# Revit family: E_Wall Junction Box_F_MEPcontent_Spelsberg_RK-RKA-ALR-AKi-R_INT-EN
name_source: partatom
category: Elektroinstallationen
revit_build: Autodesk Revit 2017 (Build: 20160225_1515(x64)
units: mm (PartAtom-declared; Revit-internal decimal feet)

## family parameters
Basisbauteil = Fläche
Beim Laden mit Abzugskörper schneiden = Nein
Bemaßung runder Anschluss = Durchmesser verwenden
Beschriftungsausrichtung beibehalten = Ja
Gemeinsam genutzt = Nein
OmniClass-Nummer = 23.80.30.14.24
OmniClass-Titel = Junction Boxes
Raumberechnungspunkt = Nein
Teiletyp = Verteilerkasten

## types (110) — shared parameters
Beschreibung = Terminal block enclosure RKK 4/07-7x4²
ETIM Article Class = EC000261
Hersteller = Spelsberg
IFCExportAs = IfcJunctionBox
IFCExportType = NOTDEFINED
Manufacturer URL = http://www.spelsberg.com
Modell = RKK 4/07-7x4²
Placeholder Height = 5 mm  [stored 0.0164042 ft]
Product Line = Spelsberg
Revit Version = 2017
Rotation U-Axis Correction = 0.00°
Rotation U-Axis Default Correction = 0.00°
Rotation V-Axis Correction = 0.00°
Rotation V-Axis Default Correction = 0.00°
Rotation W-Axis Correction = 0.00°
Rotation W-Axis Default Correction = 0.00°
URL = www.stabiplan.com
Void Diameter = 4 mm  [stored 0.0131234 ft]
zero-valued in all types: Main Screw Condition, Vorgabe-Ansicht

## per-type parameters (varying)
| type | Article Description | Body | Cap | Cap Height | Height | Horizontal Third Screw | Length | Manufacturer Art. No. | Vertical Third Screw | Width |
| AKi-R 4/136-SL | Terminal block enclosure AKi-R 4/136-SL | Color RGB 197-199-196 | Color RGB 197-199-196 | 38 mm  [stored 0.124672 ft] | 132 mm  [stored 0.433071 ft] | Nein | 600 mm | 74313601 | Ja | 300 mm |
| AKi-R 4/102-SL | Terminal block enclosure AKi-R 4/102-SL | Color RGB 197-199-196 | Color RGB 197-199-196 | 38 mm  [stored 0.124672 ft] | 132 mm  [stored 0.433071 ft] | Nein | 450 mm | 74310201 | Nein | 300 mm |
| AKi-R 4/68-SL | Terminal block enclosure AKi-R 4/68-SL | Color RGB 140-150-157 | Color RGB 140-150-157 | 38 mm  [stored 0.124672 ft] | 132 mm  [stored 0.433071 ft] | Nein | 300 mm | 74306801 | Nein | 300 mm |
| AKi-R 4/34-SL | Terminal block enclosure AKi-R 4/34-SL | Color RGB 140-150-157 | Color RGB 140-150-157 | 38 mm  [stored 0.124672 ft] | 132 mm  [stored 0.433071 ft] | Nein | 150 mm | 74303401 | Nein | 300 mm |
| AKi-R 4/136 | Terminal block enclosure AKi-R 4/136 | Color RGB 197-199-196 | Color RGB 197-199-196 | 38 mm  [stored 0.124672 ft] | 132 mm  [stored 0.433071 ft] | Nein | 600 mm | 74213601 | Ja | 300 mm |
| AKi-R 4/102 | Terminal block enclosure AKi-R 4/102 | Color RGB 197-199-196 | Color RGB 197-199-196 | 38 mm  [stored 0.124672 ft] | 132 mm  [stored 0.433071 ft] | Nein | 450 mm | 74210201 | Nein | 300 mm |
| AKi-R 4/68 | Terminal block enclosure AKi-R 4/68 | Color RGB 197-199-196 | Color RGB 197-199-196 | 38 mm  [stored 0.124672 ft] | 132 mm  [stored 0.433071 ft] | Nein | 300 mm | 74206801 | Nein | 300 mm |
| AKi-R 4/34 | Terminal block enclosure AKi-R 4/34 | Color RGB 197-199-196 | Color RGB 197-199-196 | 38 mm  [stored 0.124672 ft] | 132 mm  [stored 0.433071 ft] | Nein | 150 mm | 74203401 | Nein | 300 mm |
| AKi-R 4/136-L | Empty enclosure AKi-R 4/136-L | Color RGB 197-199-196 | Color RGB 197-199-196 | 38 mm  [stored 0.124672 ft] | 132 mm  [stored 0.433071 ft] | Nein | 600 mm | 74190401 | Ja | 300 mm |
| AKi-R 4/102-L | Empty enclosure AKi-R 4/102-L | Color RGB 140-150-157 | Color RGB 140-150-157 | 38 mm  [stored 0.124672 ft] | 132 mm  [stored 0.433071 ft] | Nein | 450 mm | 74190301 | Nein | 300 mm |
| AKi-R 4/68-L | Empty enclosure AKi-R 4/68-L | Color RGB 140-150-157 | Color RGB 140-150-157 | 38 mm  [stored 0.124672 ft] | 132 mm  [stored 0.433071 ft] | Nein | 300 mm | 74190201 | Nein | 300 mm |
| AKi-R 4/34-L | Empty enclosure AKi-R 4/34-L | Color RGB 140-150-157 | Color RGB 140-150-157 | 38 mm  [stored 0.124672 ft] | 132 mm  [stored 0.433071 ft] | Nein | 150 mm | 74190101 | Nein | 300 mm |
| ALR 3323-L | Terminal block enclosure ALR 3323-L | Color RGB 140-150-157 | Color RGB 140-150-157 | 20 mm  [stored 0.0656168 ft] | 111 mm | Nein | 230 mm  [stored 0.754593 ft] | 16091601 | Nein | 330 mm |
| ALR 2823-L | Terminal block enclosure ALR 2823-L | Color RGB 140-150-157 | Color RGB 140-150-157 | 20 mm  [stored 0.0656168 ft] | 111 mm | Nein | 230 mm  [stored 0.754593 ft] | 16091501 | Nein | 280 mm |
| ALR 2320-L | Terminal block enclosure ALR 2320-L | Color RGB 140-150-157 | Color RGB 140-150-157 | 20 mm  [stored 0.0656168 ft] | 111 mm | Nein | 200 mm  [stored 0.656168 ft] | 16091401 | Nein | 230 mm  [stored 0.754593 ft] |
| ALR 3616-L | Terminal block enclosure ALR 3616-L | Color RGB 140-150-157 | Color RGB 140-150-157 | 20 mm  [stored 0.0656168 ft] | 91 mm  [stored 0.298556 ft] | Nein | 160 mm  [stored 0.524934 ft] | 16091301 | Nein | 360 mm |
| ALR 2616-L | Terminal block enclosure ALR 2616-L | Color RGB 140-150-157 | Color RGB 140-150-157 | 20 mm  [stored 0.0656168 ft] | 91 mm  [stored 0.298556 ft] | Nein | 160 mm  [stored 0.524934 ft] | 16091201 | Nein | 260 mm  [stored 0.853018 ft] |
| ALR 1616-L | Terminal block enclosure ALR 1616-L | Color RGB 140-150-157 | Color RGB 140-150-157 | 20 mm  [stored 0.0656168 ft] | 91 mm  [stored 0.298556 ft] | Nein | 160 mm  [stored 0.524934 ft] | 16091101 | Nein | 160 mm  [stored 0.524934 ft] |
| ALR 2212-L | Terminal block enclosure ALR 2212-L | Color RGB 140-150-157 | Color RGB 140-150-157 | 20 mm  [stored 0.0656168 ft] | 81 mm  [stored 0.265748 ft] | Nein | 120 mm  [stored 0.393701 ft] | 16091001 | Nein | 220 mm  [stored 0.721785 ft] |
| ALR 1212-L | Terminal block enclosure ALR 1212-L | Color RGB 140-150-157 | Color RGB 140-150-157 | 20 mm  [stored 0.0656168 ft] | 81 mm  [stored 0.265748 ft] | Nein | 120 mm  [stored 0.393701 ft] | 16090901 | Nein | 122 mm  [stored 0.400262 ft] |
| ALR 3323-4² | Terminal block enclosure ALR 3323-4² | Color RGB 140-150-157 | Color RGB 140-150-157 | 20 mm  [stored 0.0656168 ft] | 111 mm | Nein | 230 mm  [stored 0.754593 ft] | 16041601 | Nein | 330 mm |
| ALR 2823-4² | Terminal block enclosure ALR 2823-4² | Color RGB 140-150-157 | Color RGB 140-150-157 | 20 mm  [stored 0.0656168 ft] | 111 mm | Nein | 230 mm  [stored 0.754593 ft] | 16041501 | Nein | 280 mm |
| ALR 2320-4² | Terminal block enclosure ALR 2320-4² | Color RGB 140-150-157 | Color RGB 140-150-157 | 20 mm  [stored 0.0656168 ft] | 111 mm | Nein | 200 mm  [stored 0.656168 ft] | 16041401 | Nein | 230 mm  [stored 0.754593 ft] |
| ALR 3616-4² | Terminal block enclosure ALR 3616-4² | Color RGB 140-150-157 | Color RGB 140-150-157 | 20 mm  [stored 0.0656168 ft] | 91 mm  [stored 0.298556 ft] | Nein | 160 mm  [stored 0.524934 ft] | 16041301 | Nein | 360 mm |
| ALR 2616-4² | Terminal block enclosure ALR 2616-4² | Color RGB 140-150-157 | Color RGB 140-150-157 | 20 mm  [stored 0.0656168 ft] | 91 mm  [stored 0.298556 ft] | Nein | 160 mm  [stored 0.524934 ft] | 16041201 | Nein | 260 mm  [stored 0.853018 ft] |
| ALR 1616-4² | Terminal block enclosure ALR 1616-4² | Color RGB 140-150-157 | Color RGB 140-150-157 | 20 mm  [stored 0.0656168 ft] | 91 mm  [stored 0.298556 ft] | Nein | 160 mm  [stored 0.524934 ft] | 16041101 | Nein | 160 mm  [stored 0.524934 ft] |
| ALR 2212-4² | Terminal block enclosure ALR 2212-4² | Color RGB 140-150-157 | Color RGB 140-150-157 | 20 mm  [stored 0.0656168 ft] | 81 mm  [stored 0.265748 ft] | Nein | 120 mm  [stored 0.393701 ft] | 16041001 | Nein | 220 mm  [stored 0.721785 ft] |
| ALR 1212-4² | Terminal block enclosure ALR 1212-4² | Color RGB 140-150-157 | Color RGB 140-150-157 | 20 mm  [stored 0.0656168 ft] | 81 mm  [stored 0.265748 ft] | Nein | 120 mm  [stored 0.393701 ft] | 16040901 | Nein | 122 mm  [stored 0.400262 ft] |
| ALR 1010-4² | Terminal block enclosure ALR 1010-4² | Color RGB 140-150-157 | Color RGB 140-150-157 | 20 mm  [stored 0.0656168 ft] | 81 mm  [stored 0.265748 ft] | Nein | 100 mm  [stored 0.328084 ft] | 16040801 | Nein | 100 mm  [stored 0.328084 ft] |
| ALR 1808-4² | Terminal block enclosure ALR 1808-4² | Color RGB 140-150-157 | Color RGB 140-150-157 | 15 mm  [stored 0.0492126 ft] | 57 mm  [stored 0.187008 ft] | Nein | 80 mm  [stored 0.262467 ft] | 16040701 | Nein | 175 mm  [stored 0.574147 ft] |
| ALR 1308-4² | Terminal block enclosure ALR 1308-4² | Color RGB 140-150-157 | Color RGB 140-150-157 | 15 mm  [stored 0.0492126 ft] | 57 mm  [stored 0.187008 ft] | Nein | 80 mm  [stored 0.262467 ft] | 16040601 | Nein | 125 mm  [stored 0.410105 ft] |
| ALR 88-4² | Terminal block enclosure ALR 88-4² | Color RGB 140-150-157 | Color RGB 140-150-157 | 15 mm  [stored 0.0492126 ft] | 57 mm  [stored 0.187008 ft] | Nein | 80 mm  [stored 0.262467 ft] | 16040501 | Nein | 75 mm |
| RKA 4/136-L | Empty enclosure RKA 4/136-L | Color RGB 140-150-157 | Color RGB 140-150-157 | 39 mm  [stored 0.127953 ft] | 132 mm  [stored 0.433071 ft] | Nein | 600 mm | 62990401 | Ja | 300 mm |
| RKA 4/102-L | Empty enclosure RKA 4/102-L | Color RGB 140-150-157 | Color RGB 140-150-157 | 39 mm  [stored 0.127953 ft] | 132 mm  [stored 0.433071 ft] | Nein | 450 mm | 62990301 | Nein | 300 mm |
| RKA 4/68-L | Empty enclosure RKA 4/68-L | Color RGB 140-150-157 | Color RGB 140-150-157 | 39 mm  [stored 0.127953 ft] | 132 mm  [stored 0.433071 ft] | Nein | 300 mm | 62990201 | Nein | 300 mm |
| RKA 4/34-L | Empty enclosure RKA 4/34-L | Color RGB 140-150-157 | Color RGB 140-150-157 | 39 mm  [stored 0.127953 ft] | 132 mm  [stored 0.433071 ft] | Nein | 150 mm | 62990101 | Nein | 300 mm |
| RKA 4/136-136x4² | Terminal block enclosure RKA 4/136-136x4² | Color RGB 197-199-196 | Color RGB 197-199-196 | 39 mm  [stored 0.127953 ft] | 132 mm  [stored 0.433071 ft] | Nein | 600 mm | 62513601 | Ja | 300 mm |
| RKA 4/102-102x4² | Terminal block enclosure RKA 4/102-102x4² | Color RGB 197-199-196 | Color RGB 197-199-196 | 39 mm  [stored 0.127953 ft] | 132 mm  [stored 0.433071 ft] | Nein | 450 mm | 62510201 | Nein | 300 mm |
| RKA 4/68-68x4² | Terminal block enclosure RKA 4/68-68x4² | Color RGB 197-199-196 | Color RGB 197-199-196 | 39 mm  [stored 0.127953 ft] | 132 mm  [stored 0.433071 ft] | Nein | 300 mm | 62506801 | Nein | 300 mm |
| RKA 4/34-34x4² | Terminal block enclosure RKA 4/34-34x4² | Color RGB 197-199-196 | Color RGB 197-199-196 | 39 mm  [stored 0.127953 ft] | 132 mm  [stored 0.433071 ft] | Nein | 150 mm | 62503401 | Nein | 300 mm |
| RKA 4/136 SL-136x4² | Terminal block enclosure RKA 4/136 SL-136x4² | Color RGB 197-199-196 | Color RGB 197-199-196 | 39 mm  [stored 0.127953 ft] | 132 mm  [stored 0.433071 ft] | Nein | 600 mm | 62013601 | Ja | 300 mm |
| RKA 4/102 SL-102x4² | Terminal block enclosure RKA 4/102 SL-102x4² | Color RGB 197-199-196 | Color RGB 197-199-196 | 39 mm  [stored 0.127953 ft] | 132 mm  [stored 0.433071 ft] | Nein | 450 mm | 62010201 | Nein | 300 mm |
| RKA 4/68 SL-68x4² | Terminal block enclosure RKA 4/68 SL-68x4² | Color RGB 197-199-196 | Color RGB 197-199-196 | 39 mm  [stored 0.127953 ft] | 132 mm  [stored 0.433071 ft] | Nein | 300 mm | 62006801 | Nein | 300 mm |
| RKA 4/34 SL-34x4² | Terminal block enclosure RKA 4/34 SL-34x4² | Color RGB 197-199-196 | Color RGB 197-199-196 | 39 mm  [stored 0.127953 ft] | 132 mm  [stored 0.433071 ft] | Nein | 150 mm | 62003401 | Nein | 300 mm |
| RKi 4/07-L | Empty enclosure RKi 4/07-L | Color RGB 197-199-196 | Color RGB 197-199-196 | 24 mm  [stored 0.0787402 ft] | 90 mm  [stored 0.295276 ft] | Nein | 110 mm  [stored 0.360892 ft] | 63990701 | Nein | 110 mm  [stored 0.360892 ft] |
| RKi 4/50-L | Empty enclosure RKi 4/50-L | Color RGB 197-199-196 | Color RGB 197-199-196 | 39 mm  [stored 0.127953 ft] | 111 mm | Ja | 254 mm | 63695001 | Nein | 360 mm |
| RKi 4/100-L | Empty enclosure RKi 4/100-L | Color RGB 140-150-157 | Color RGB 140-150-157 | 39 mm  [stored 0.127953 ft] | 111 mm | Ja | 254 mm | 63692201 | Nein | 360 mm |
| RKi 4/18-L | Empty enclosure RKi 4/18-L | Color RGB 140-150-157 | Color RGB 140-150-157 | 19 mm  [stored 0.062336 ft] | 90 mm  [stored 0.295276 ft] | Nein | 180 mm  [stored 0.590551 ft] | 63691201 | Nein | 182 mm  [stored 0.597113 ft] |
| RKi 4/34-L | Empty enclosure RKi 4/34-L | Color RGB 197-199-196 | Color RGB 197-199-196 | 19 mm  [stored 0.062336 ft] | 90 mm  [stored 0.295276 ft] | Nein | 180 mm  [stored 0.590551 ft] | 63591701 | Nein | 254 mm |
| RKi 4/25-L | Empty enclosure RKi 4/25-L | Color RGB 197-199-196 | Color RGB 197-199-196 | 19 mm  [stored 0.062336 ft] | 90 mm  [stored 0.295276 ft] | Nein | 180 mm  [stored 0.590551 ft] | 63591601 | Nein | 254 mm |
| RKi 4/18 K-L | Empty enclosure RKi 4/18 K-L | Color RGB 197-199-196 | Color RGB 197-199-196 | 19 mm  [stored 0.062336 ft] | 90 mm  [stored 0.295276 ft] | Nein | 110 mm  [stored 0.360892 ft] | 63591201 | Nein | 180 mm  [stored 0.590551 ft] |
| RKi 4/100-100x4² | Terminal block enclosure RKi 4/100-100x4² | Color RGB 140-150-157 | Color RGB 140-150-157 | 39 mm  [stored 0.127953 ft] | 111 mm | Ja | 254 mm | 63510001 | Nein | 360 mm |
| RKi 4/50-50x4² | Terminal block enclosure RKi 4/50-50x4² | Color RGB 197-199-196 | Color RGB 197-199-196 | 39 mm  [stored 0.127953 ft] | 111 mm | Ja | 254 mm | 63505001 | Nein | 360 mm |
| RKi 4/34-34x4² | Terminal block enclosure RKi 4/34-34x4² | Color RGB 197-199-196 | Color RGB 197-199-196 | 19 mm  [stored 0.062336 ft] | 90 mm  [stored 0.295276 ft] | Nein | 180 mm  [stored 0.590551 ft] | 63503401 | Nein | 254 mm |
| RKi 4/25-25x4² | Terminal block enclosure RKi 4/25-25x4² | Color RGB 197-199-196 | Color RGB 197-199-196 | 19 mm  [stored 0.062336 ft] | 90 mm  [stored 0.295276 ft] | Nein | 180 mm  [stored 0.590551 ft] | 63502501 | Nein | 254 mm |
| RKi 4/18-18x4² | Terminal block enclosure RKi 4/18-18x4² | Color RGB 140-150-157 | Color RGB 140-150-157 | 19 mm  [stored 0.062336 ft] | 90 mm  [stored 0.295276 ft] | Nein | 180 mm  [stored 0.590551 ft] | 63501901 | Nein | 182 mm  [stored 0.597113 ft] |
| RKi 4/18 K-18x4² | Terminal block enclosure RKi 4/18 K-18x4² | Color RGB 197-199-196 | Color RGB 197-199-196 | 19 mm  [stored 0.062336 ft] | 90 mm  [stored 0.295276 ft] | Nein | 110 mm  [stored 0.360892 ft] | 63501801 | Nein | 180 mm  [stored 0.590551 ft] |
| RKi 4/12-12x4² | Terminal block enclosure RKi 4/12-12x4² | Color RGB 140-150-157 | Color RGB 140-150-157 | 15 mm  [stored 0.0492126 ft] | 75 mm | Nein | 130 mm  [stored 0.426509 ft] | 63501201 | Nein | 130 mm  [stored 0.426509 ft] |
| RKi 4/07-7x4² | Terminal block enclosure RKi 4/07-7x4² | Color RGB 197-199-196 | Color RGB 197-199-196 | 40 mm  [stored 0.131234 ft] | 90 mm  [stored 0.295276 ft] | Nein | 110 mm  [stored 0.360892 ft] | 63500701 | Nein | 110 mm  [stored 0.360892 ft] |
| RKi 4/12-L | Empty enclosure RKi 4/12-L | Color RGB 140-150-157 | Color RGB 140-150-157 | 15 mm  [stored 0.0492126 ft] | 75 mm | Nein | 130 mm  [stored 0.426509 ft] | 63390601 | Nein | 130 mm  [stored 0.426509 ft] |
| RKi 4/100 SL-100x4² | Terminal block enclosure RKi 4/100 SL-100x4² | Color RGB 197-199-196 | Color RGB 197-199-196 | 39 mm  [stored 0.127953 ft] | 111 mm | Ja | 254 mm | 63010001 | Nein | 360 mm |
| RKi 4/50 SL-50x4² | Terminal block enclosure RKi 4/50 SL-50x4² | Color RGB 197-199-196 | Color RGB 197-199-196 | 39 mm  [stored 0.127953 ft] | 111 mm | Ja | 254 mm | 63005001 | Nein | 360 mm |
| RKi 4/34 SL-34x4² | Terminal block enclosure RKi 4/34 SL-34x4² | Color RGB 197-199-196 | Color RGB 197-199-196 | 16 mm  [stored 0.0524934 ft] | 90 mm  [stored 0.295276 ft] | Nein | 180 mm  [stored 0.590551 ft] | 63003401 | Nein | 254 mm |
| RKi 4/25 SL-25x4² | Terminal block enclosure RKi 4/25 SL-25x4² | Color RGB 197-199-196 | Color RGB 197-199-196 | 16 mm  [stored 0.0524934 ft] | 90 mm  [stored 0.295276 ft] | Nein | 180 mm  [stored 0.590551 ft] | 63002501 | Nein | 254 mm |
| RKi 4/18 SL-18x4² | Terminal block enclosure RKi 4/18 SL-18x4² | Color RGB 197-199-196 | Color RGB 197-199-196 | 18 mm  [stored 0.0590551 ft] | 90 mm  [stored 0.295276 ft] | Nein | 180 mm  [stored 0.590551 ft] | 63001901 | Nein | 182 mm  [stored 0.597113 ft] |
| RKi 4/18 KSL-18x4² | Terminal block enclosure RKi 4/18 KSL-18x4² | Color RGB 197-199-196 | Color RGB 197-199-196 | 18 mm  [stored 0.0590551 ft] | 90 mm  [stored 0.295276 ft] | Nein | 110 mm  [stored 0.360892 ft] | 63001801 | Nein | 180 mm  [stored 0.590551 ft] |
| RKi 4/12 SL-12x4² | Terminal block enclosure RKi 4/12 SL-12x4² | Color RGB 197-199-196 | Color RGB 197-199-196 | 16 mm  [stored 0.0524934 ft] | 75 mm | Nein | 130 mm  [stored 0.426509 ft] | 63001201 | Nein | 130 mm  [stored 0.426509 ft] |
| RKi 4/07 SL-7x4² | Terminal block enclosure RKi 4/07 SL-7x4² | Color RGB 197-199-196 | Color RGB 197-199-196 | 40 mm  [stored 0.131234 ft] | 90 mm  [stored 0.295276 ft] | Nein | 110 mm  [stored 0.360892 ft] | 63000701 | Nein | 110 mm  [stored 0.360892 ft] |
| RK 4/100-L | Empty enclosure RK 4/100-L | Color RGB 140-150-157 | Color RGB 140-150-157 | 39 mm  [stored 0.127953 ft] | 111 mm | Ja | 254 mm | 62692201 | Nein | 360 mm |
| RK 4/34-L | Empty enclosure RK 4/34-L | Color RGB 197-199-196 | Color RGB 197-199-196 | 18 mm  [stored 0.0590551 ft] | 90 mm  [stored 0.295276 ft] | Nein | 180 mm  [stored 0.590551 ft] | 62591701 | Nein | 254 mm |
| RK 4/25-L | Empty enclosure RK 4/25-L | Color RGB 197-199-196 | Color RGB 197-199-196 | 18 mm  [stored 0.0590551 ft] | 90 mm  [stored 0.295276 ft] | Nein | 180 mm  [stored 0.590551 ft] | 62591601 | Nein | 254 mm |
| RK 4/07-L | Empty enclosure RK 4/07-L | Color RGB 197-199-196 | Color RGB 197-199-196 | 25 mm  [stored 0.082021 ft] | 90 mm  [stored 0.295276 ft] | Nein | 110 mm  [stored 0.360892 ft] | 61990701 | Nein | 110 mm  [stored 0.360892 ft] |
| RK 4/50-L | Empty enclosure RK 4/50-L | Color RGB 197-199-196 | Color RGB 197-199-196 | 39 mm  [stored 0.127953 ft] | 111 mm | Ja | 254 mm | 61695001 | Nein | 360 mm |
| RK 4/18-L | Empty enclosure RK 4/18-L | Color RGB 140-150-157 | Color RGB 140-150-157 | 18 mm  [stored 0.0590551 ft] | 90 mm  [stored 0.295276 ft] | Nein | 180 mm  [stored 0.590551 ft] | 61691201 | Nein | 182 mm  [stored 0.597113 ft] |
| RK 4/18 K-L | Empty enclosure RK 4/18 K-L | Color RGB 197-199-196 | Color RGB 197-199-196 | 18 mm  [stored 0.0590551 ft] | 90 mm  [stored 0.295276 ft] | Nein | 110 mm  [stored 0.360892 ft] | 61591201 | Nein | 180 mm  [stored 0.590551 ft] |
| RK 4/100-100x4² | Terminal block enclosure RK 4/100-100x4² | Color RGB 140-150-157 | Color RGB 140-150-157 | 39 mm  [stored 0.127953 ft] | 111 mm | Ja | 254 mm | 61510001 | Nein | 360 mm |
| RK 4/50-50x4² | Terminal block enclosure RK 4/50-50x4² | Color RGB 197-199-196 | Color RGB 197-199-196 | 39 mm  [stored 0.127953 ft] | 111 mm | Ja | 254 mm | 61505001 | Nein | 360 mm |
| RK 4/34-34x4² | Terminal block enclosure RK 4/34-34x4² | Color RGB 197-199-196 | Color RGB 197-199-196 | 18 mm  [stored 0.0590551 ft] | 90 mm  [stored 0.295276 ft] | Nein | 180 mm  [stored 0.590551 ft] | 61503401 | Nein | 254 mm |
| RK 4/25-25x4² | Terminal block enclosure RK 4/25-25x4² | Color RGB 197-199-196 | Color RGB 197-199-196 | 18 mm  [stored 0.0590551 ft] | 90 mm  [stored 0.295276 ft] | Nein | 180 mm  [stored 0.590551 ft] | 61502501 | Nein | 254 mm |
| RK 4/18-18x4² | Terminal block enclosure RK 4/18-18x4² | Color RGB 140-150-157 | Color RGB 140-150-157 | 18 mm  [stored 0.0590551 ft] | 90 mm  [stored 0.295276 ft] | Nein | 180 mm  [stored 0.590551 ft] | 61501901 | Nein | 182 mm  [stored 0.597113 ft] |
| RK 4/18 K-18x4² | Terminal block enclosure RK 4/18 K-18x4² | Color RGB 140-150-157 | Color RGB 140-150-157 | 18 mm  [stored 0.0590551 ft] | 90 mm  [stored 0.295276 ft] | Nein | 110 mm  [stored 0.360892 ft] | 61501801 | Nein | 180 mm  [stored 0.590551 ft] |
| RK 4/12-12x4² | Terminal block enclosure RK 4/12-12x4² | Color RGB 140-150-157 | Color RGB 140-150-157 | 16 mm  [stored 0.0524934 ft] | 75 mm | Nein | 130 mm  [stored 0.426509 ft] | 61501201 | Nein | 130 mm  [stored 0.426509 ft] |
| RK 4/07-7x4² | Terminal block enclosure RK 4/07-7x4² | Color RGB 197-199-196 | Color RGB 197-199-196 | 40 mm  [stored 0.131234 ft] | 90 mm  [stored 0.295276 ft] | Nein | 110 mm  [stored 0.360892 ft] | 61500701 | Nein | 110 mm  [stored 0.360892 ft] |
| RK 4/12-L | Empty enclosure RK 4/12-L | Color RGB 140-150-157 | Color RGB 140-150-157 | 15 mm  [stored 0.0492126 ft] | 75 mm | Nein | 130 mm  [stored 0.426509 ft] | 61390601 | Nein | 130 mm  [stored 0.426509 ft] |
| RK 4/100 SL-100x4² | Terminal block enclosure RK 4/100 SL-100x4² | Color RGB 197-199-196 | Color RGB 197-199-196 | 39 mm  [stored 0.127953 ft] | 111 mm | Ja | 254 mm | 61010001 | Nein | 360 mm |
| RK 4/50 SL-50x4² | Terminal block enclosure RK 4/50 SL-50x4² | Color RGB 197-199-196 | Color RGB 197-199-196 | 39 mm  [stored 0.127953 ft] | 111 mm | Ja | 254 mm | 61005001 | Nein | 360 mm |
| RK 4/34 SL-34x4² | Terminal block enclosure RK 4/34 SL-34x4² | Color RGB 197-199-196 | Color RGB 197-199-196 | 18 mm  [stored 0.0590551 ft] | 90 mm  [stored 0.295276 ft] | Nein | 180 mm  [stored 0.590551 ft] | 61003401 | Nein | 254 mm |
| RK 4/25 SL-25x4² | Terminal block enclosure RK 4/25 SL-25x4² | Color RGB 197-199-196 | Color RGB 197-199-196 | 18 mm  [stored 0.0590551 ft] | 90 mm  [stored 0.295276 ft] | Nein | 180 mm  [stored 0.590551 ft] | 61002501 | Nein | 254 mm |
| RK 4/18 SL-18x4² | Terminal block enclosure RK 4/18 SL-18x4² | Color RGB 197-199-196 | Color RGB 197-199-196 | 18 mm  [stored 0.0590551 ft] | 90 mm  [stored 0.295276 ft] | Nein | 180 mm  [stored 0.590551 ft] | 61001901 | Nein | 182 mm  [stored 0.597113 ft] |
| RK 4/18 KSL-18x4² | Terminal block enclosure RK 4/18 KSL-18x4² | Color RGB 197-199-196 | Color RGB 197-199-196 | 18 mm  [stored 0.0590551 ft] | 90 mm  [stored 0.295276 ft] | Nein | 110 mm  [stored 0.360892 ft] | 61001801 | Nein | 180 mm  [stored 0.590551 ft] |
| RK 4/12 SL-12x4² | Terminal block enclosure RK 4/12 SL-12x4² | Color RGB 197-199-196 | Color RGB 197-199-196 | 15 mm  [stored 0.0492126 ft] | 75 mm | Nein | 130 mm  [stored 0.426509 ft] | 61001201 | Nein | 130 mm  [stored 0.426509 ft] |
| RK 4/07 SL-7x4² | Terminal block enclosure RK 4/07 SL-7x4² | Color RGB 197-199-196 | Color RGB 197-199-196 | 40 mm  [stored 0.131234 ft] | 90 mm  [stored 0.295276 ft] | Nein | 110 mm  [stored 0.360892 ft] | 61000701 | Nein | 110 mm  [stored 0.360892 ft] |
| RKKi 4/10-10x4² | Terminal block enclosure RKKi 4/10-10x4² | Color RGB 197-199-196 | Color RGB 197-199-196 | 16 mm  [stored 0.0524934 ft] | 57 mm  [stored 0.187008 ft] | Nein | 94 mm  [stored 0.308399 ft] | 63740401 | Nein | 94 mm  [stored 0.308399 ft] |
| RKKi 4/08-8x4² | Terminal block enclosure RKKi 4/08-8x4² | Color RGB 197-199-196 | Color RGB 197-199-196 | 16 mm  [stored 0.0524934 ft] | 57 mm  [stored 0.187008 ft] | Nein | 94 mm  [stored 0.308399 ft] | 63640401 | Nein | 94 mm  [stored 0.308399 ft] |
| RKKi 4/05-5x4² | Terminal block enclosure RKKi 4/05-5x4² | Color RGB 197-199-196 | Color RGB 197-199-196 | 16 mm  [stored 0.0524934 ft] | 57 mm  [stored 0.187008 ft] | Nein | 65 mm  [stored 0.213255 ft] | 63540401 | Nein | 94 mm  [stored 0.308399 ft] |
| RKKi 4/22-22x4² | Terminal block enclosure RKKi 4/22-22x4² | Color RGB 197-199-196 | Color RGB 197-199-196 | 16 mm  [stored 0.0524934 ft] | 57 mm  [stored 0.187008 ft] | Nein | 94 mm  [stored 0.308399 ft] | 63440401 | Nein | 180 mm  [stored 0.590551 ft] |
| RKKi 4/15-15x4² | Terminal block enclosure RKKi 4/15-15x4² | Color RGB 197-199-196 | Color RGB 197-199-196 | 16 mm  [stored 0.0524934 ft] | 57 mm  [stored 0.187008 ft] | Nein | 94 mm  [stored 0.308399 ft] | 63240401 | Nein | 130 mm  [stored 0.426509 ft] |
| RKKi 4/18-18x4² | Terminal block enclosure RKKi 4/18-18x4² | Color RGB 197-199-196 | Color RGB 197-199-196 | 16 mm  [stored 0.0524934 ft] | 57 mm  [stored 0.187008 ft] | Nein | 94 mm  [stored 0.308399 ft] | 63041801 | Nein | 180 mm  [stored 0.590551 ft] |
| RKKi 4/12 XL-12x4² | Terminal block enclosure RKKi 4/12 XL-12x4² | Color RGB 197-199-196 | Color RGB 197-199-196 | 16 mm  [stored 0.0524934 ft] | 57 mm  [stored 0.187008 ft] | Nein | 94 mm  [stored 0.308399 ft] | 63041201 | Nein | 130 mm  [stored 0.426509 ft] |
| RKKi 4/07-7x4² | Terminal block enclosure RKKi 4/07-7x4² | Color RGB 197-199-196 | Color RGB 197-199-196 | 16 mm  [stored 0.0524934 ft] | 57 mm  [stored 0.187008 ft] | Nein | 94 mm  [stored 0.308399 ft] | 63040701 | Nein | 94 mm  [stored 0.308399 ft] |
| RKKi 4/12-12x4² | Terminal block enclosure RKKi 4/12-12x4² | Color RGB 197-199-196 | Color RGB 197-199-196 | 16 mm  [stored 0.0524934 ft] | 66 mm  [stored 0.216535 ft] | Nein | 110 mm  [stored 0.360892 ft] | 63040401 | Nein | 110 mm  [stored 0.360892 ft] |
| RKK 4/22-22x4² | Terminal block enclosure RKK 4/22-22x4² | Color RGB 197-199-196 | Color RGB 197-199-196 | 16 mm  [stored 0.0524934 ft] | 57 mm  [stored 0.187008 ft] | Nein | 94 mm  [stored 0.308399 ft] | 61440401 | Nein | 180 mm  [stored 0.590551 ft] |
| RKK 4/15-15x4² | Terminal block enclosure RKK 4/15-15x4² | Color RGB 197-199-196 | Color RGB 197-199-196 | 16 mm  [stored 0.0524934 ft] | 57 mm  [stored 0.187008 ft] | Nein | 94 mm  [stored 0.308399 ft] | 61240401 | Nein | 130 mm  [stored 0.426509 ft] |
| RKK 4/12-12x4² | Terminal block enclosure RKK 4/12-12x4² | Color RGB 197-199-196 | Color RGB 197-199-196 | 16 mm  [stored 0.0524934 ft] | 66 mm  [stored 0.216535 ft] | Nein | 110 mm  [stored 0.360892 ft] | 61040401 | Nein | 110 mm  [stored 0.360892 ft] |
| RKK 4/10-10x4² | Terminal block enclosure RKK 4/10-10x4² | Color RGB 197-199-196 | Color RGB 197-199-196 | 16 mm  [stored 0.0524934 ft] | 57 mm  [stored 0.187008 ft] | Nein | 94 mm  [stored 0.308399 ft] | 60740401 | Nein | 94 mm  [stored 0.308399 ft] |
| RKK 4/08-8x4² | Terminal block enclosure RKK 4/08-8x4² | Color RGB 197-199-196 | Color RGB 197-199-196 | 16 mm  [stored 0.0524934 ft] | 57 mm  [stored 0.187008 ft] | Nein | 94 mm  [stored 0.308399 ft] | 60640401 | Nein | 94 mm  [stored 0.308399 ft] |
| RKK 4/05-5x4² | Terminal block enclosure RKK 4/05-5x4² | Color RGB 197-199-196 | Color RGB 197-199-196 | 16 mm  [stored 0.0524934 ft] | 57 mm  [stored 0.187008 ft] | Nein | 65 mm  [stored 0.213255 ft] | 60540401 | Nein | 94 mm  [stored 0.308399 ft] |
| RKK 4/18-18x4² | Terminal block enclosure RKK 4/18-18x4² | Color RGB 197-199-196 | Color RGB 197-199-196 | 16 mm  [stored 0.0524934 ft] | 57 mm  [stored 0.187008 ft] | Nein | 94 mm  [stored 0.308399 ft] | 60041801 | Nein | 180 mm  [stored 0.590551 ft] |
| RKK 4/12 XL-12x4² | Terminal block enclosure RKK 4/12 XL-12x4² | Color RGB 197-199-196 | Color RGB 197-199-196 | 16 mm  [stored 0.0524934 ft] | 57 mm  [stored 0.187008 ft] | Nein | 94 mm  [stored 0.308399 ft] | 60041201 | Nein | 130 mm  [stored 0.426509 ft] |
| RKK 4/07-7x4² | Terminal block enclosure RKK 4/07-7x4² | Color RGB 197-199-196 | Color RGB 197-199-196 | 16 mm  [stored 0.0524934 ft] | 57 mm  [stored 0.187008 ft] | Nein | 94 mm  [stored 0.308399 ft] | 60040701 | Nein | 94 mm  [stored 0.308399 ft] |

note: column(s) folded — value = type name in every type: Article Type

note: [stored X ft] marks values corroborated as IEEE doubles in the binary element streams (Revit-internal decimal feet)

## geometry (parser evidence)
native form markers: Sweep x17
no freeform markers — native parametric forms only
